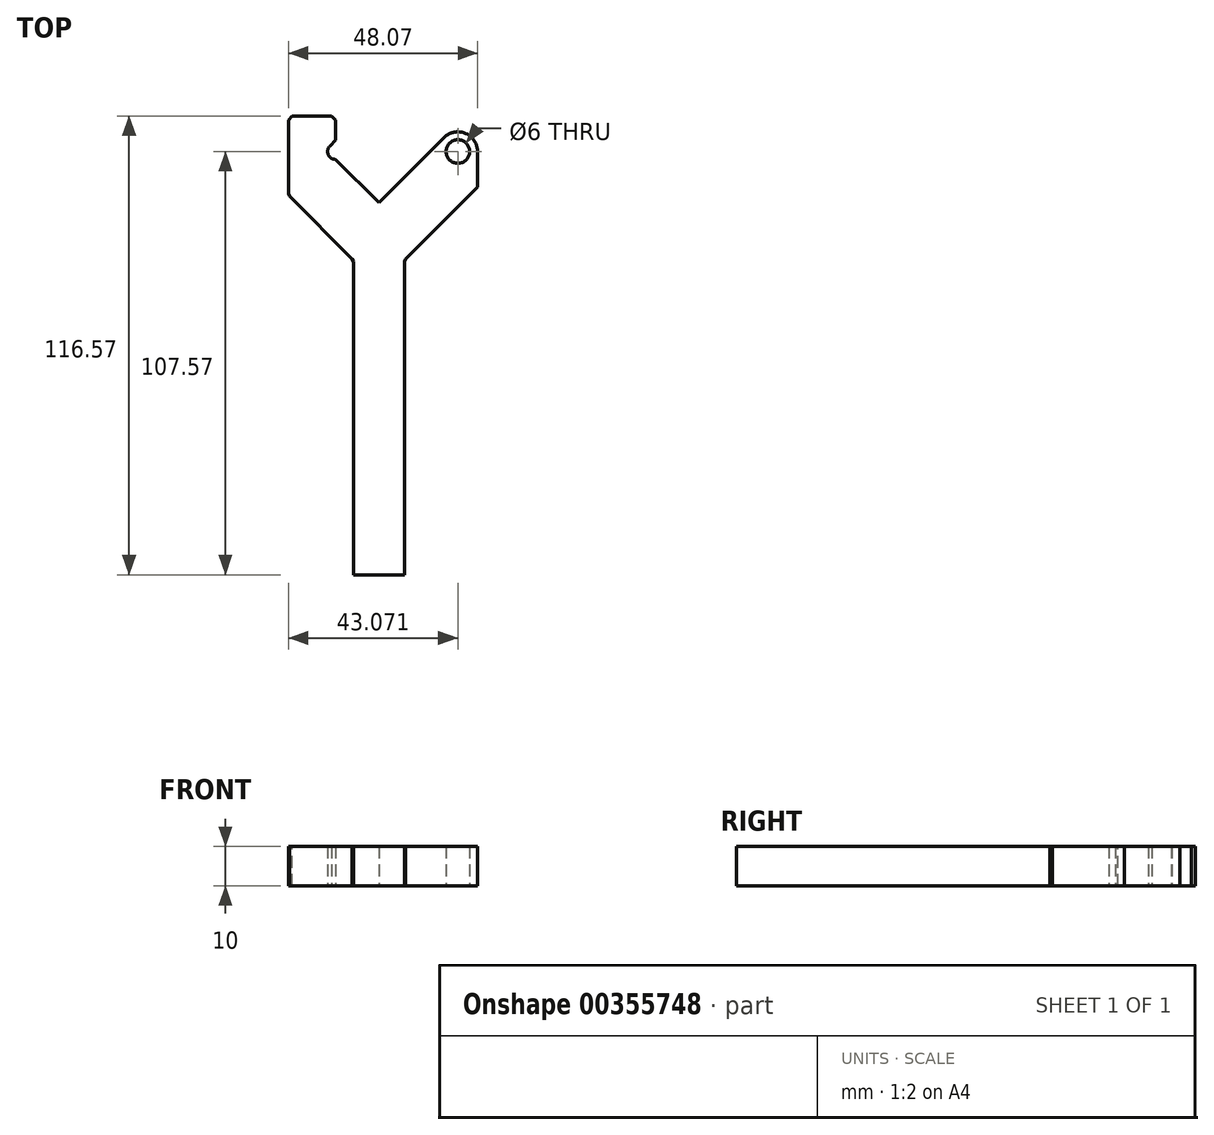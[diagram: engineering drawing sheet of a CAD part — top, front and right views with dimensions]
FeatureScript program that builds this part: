
annotation { "Feature Type Name" : "Feature", "Feature Type Description" : "" }
export const myFeature = defineFeature(function(context is Context, id is Id, definition is map)
    precondition{}
    {
        {
            var Q0;
            Q0=qCreatedBy(makeId("Top.planeOp"),FACE);
            var sketch = newSketch(context, id + "F0", { "sketchPlane" : qUnion([Q0])});
            skLineSegment(sketch, "E0", {"start": v(0, 0) * mm, "end": v(18, 18) * mm});
            skLineSegment(sketch, "E1", {"start": v(18, 18) * mm, "end": v(25.07, 18) * mm});
            skLineSegment(sketch, "E2", {"start": v(25.07, 18) * mm, "end": v(25.07, 4) * mm});
            skLineSegment(sketch, "E3", {"start": v(25.07, 4) * mm, "end": v(6.5, -14.57) * mm});
            skLineSegment(sketch, "E4", {"start": v(6.5, -14.57) * mm, "end": v(6.5, -94.57) * mm});
            skLineSegment(sketch, "E5", {"start": v(6.5, -94.57) * mm, "end": v(-6.5, -94.57) * mm});
            skLineSegment(sketch, "E6", {"start": v(-6.5, -94.57) * mm, "end": v(-6.5, -14.57) * mm});
            skLineSegment(sketch, "E7", {"start": v(-6.5, -14.57) * mm, "end": v(-23, 1.93) * mm});
            skLineSegment(sketch, "E8", {"start": v(-23, 1.93) * mm, "end": v(-23, 22) * mm});
            skLineSegment(sketch, "E9", {"start": v(-23, 22) * mm, "end": v(-11, 22) * mm});
            skLineSegment(sketch, "E10", {"start": v(-11, 22) * mm, "end": v(-11, 15.85) * mm});
            skArc(sketch, "E11", {"start": v(-12.44, 14.41) * mm, "mid": v(-12.87, 12.22) * mm, "end": v(-11, 11) * mm});
            skLineSegment(sketch, "E12", {"start": v(-11, 11) * mm, "end": v(0, 0) * mm});
            skCircle(sketch, "E13", {"center": v(20.07, 13) * mm, "radius": 3 * mm});
            skLineSegment(sketch, "E14", {"start": v(-11, 15.85) * mm, "end": v(-12.44, 14.41) * mm});
            skPoint(sketch, "E15.orphan", {"position": v(-11, 15) * mm});
            skLineSegment(sketch, "E16", {"start": v(-6.5, -14.57) * mm, "end": v(6.5, -14.57) * mm, "construction": true});
            skSolve(sketch);
        }
        {
            var Q0;
            Q0=makeQuery(id+"F0.imprint","IMPRINT",FACE,{"disambiguationData":[TD([[makeQuery(id+"F0.imprint","IMPRINT",EDGE,{"derivedFrom":sQuery(id+"F0.wireOp",EDGE,"E0")}),-1.0]])]});
            extrude(context, id + "F1", {"entities" : qUnion([Q0]), "depth" : 10 * mm});
        }
        {
            var Q0;
            Q0=makeQuery(id+"F1.opExtrude","SWEPT_EDGE",EDGE,{"disambiguationData":[OSD([sQuery(id+"F0.wireOp",EDGE,"E0"),sQuery(id+"F0.wireOp",EDGE,"E1")])]});
            fillet(context, id + "F2", {"entities" : qUnion([Q0]), "radius" : 5 * mm, "tangentPropagation" : true, "allowEdgeOverflow" : false});
        }
        {
            var Q0;
            Q0=makeQuery(id+"F1.opExtrude","SWEPT_EDGE",EDGE,{"disambiguationData":[OSD([sQuery(id+"F0.wireOp",EDGE,"E1"),sQuery(id+"F0.wireOp",EDGE,"E2")])]});
            fillet(context, id + "F3", {"entities" : qUnion([Q0]), "radius" : 5 * mm, "tangentPropagation" : true, "allowEdgeOverflow" : false});
        }
        {
            var Q0;
            Q0=makeQuery(id+"F1.opExtrude","SWEPT_EDGE",EDGE,{"disambiguationData":[OSD([sQuery(id+"F0.wireOp",EDGE,"E9"),sQuery(id+"F0.wireOp",EDGE,"E10")])]});
            var Q1;
            Q1=makeQuery(id+"F1.opExtrude","SWEPT_EDGE",EDGE,{"disambiguationData":[OSD([sQuery(id+"F0.wireOp",EDGE,"E8"),sQuery(id+"F0.wireOp",EDGE,"E9")])]});
            var Q2;
            Q2=makeQuery(id+"F1.opExtrude","SWEPT_EDGE",EDGE,{"disambiguationData":[OSD([sQuery(id+"F0.wireOp",EDGE,"E7"),sQuery(id+"F0.wireOp",EDGE,"E8")])]});
            var Q3;
            Q3=makeQuery(id+"F1.opExtrude","SWEPT_EDGE",EDGE,{"disambiguationData":[OSD([sQuery(id+"F0.wireOp",EDGE,"E6"),sQuery(id+"F0.wireOp",EDGE,"E7")])]});
            var Q4;
            Q4=makeQuery(id+"F1.opExtrude","SWEPT_EDGE",EDGE,{"disambiguationData":[OSD([sQuery(id+"F0.wireOp",EDGE,"E3"),sQuery(id+"F0.wireOp",EDGE,"E4")])]});
            chamfer(context, id + "F4", {"entities" : qUnion([Q0, Q1, Q2, Q3, Q4]), "width" : 1 * mm, "tangentPropagation" : true});
        }
    });
